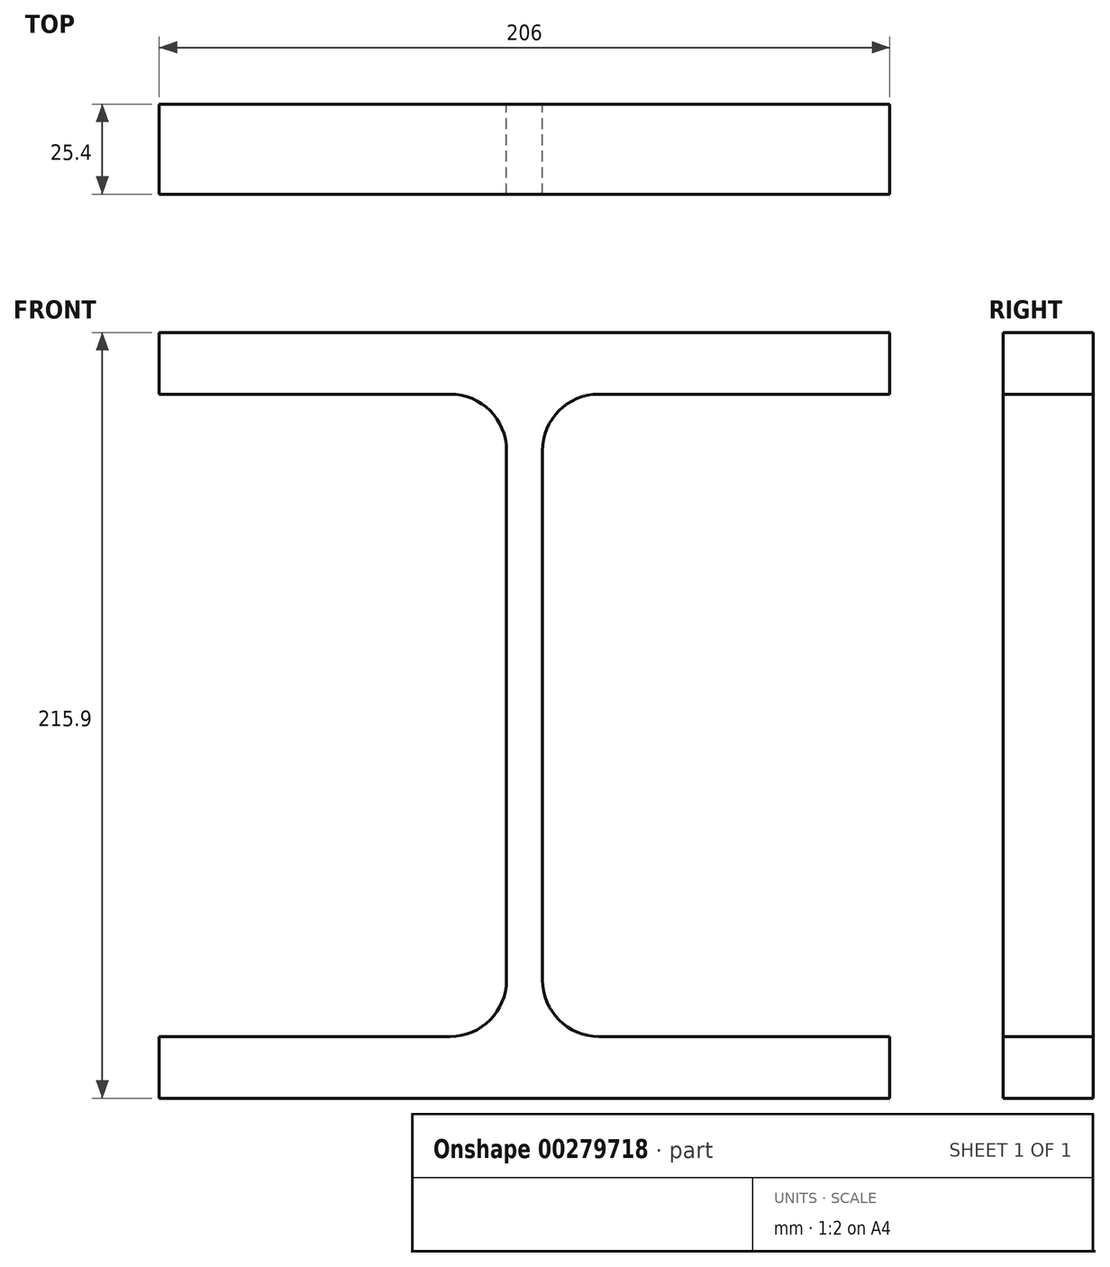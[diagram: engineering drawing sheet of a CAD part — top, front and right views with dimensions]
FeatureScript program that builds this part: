
annotation { "Feature Type Name" : "Feature", "Feature Type Description" : "" }
export const myFeature = defineFeature(function(context is Context, id is Id, definition is map)
    precondition{}
    {
        {
            var Q0;
            Q0=qCreatedBy(makeId("Front.planeOp"),FACE);
            var sketch = newSketch(context, id + "F0", { "sketchPlane" : qUnion([Q0])});
            skLineSegment(sketch, "E0.bottom", {"start": v(-103, 107.95) * mm, "end": v(103, 107.95) * mm});
            skLineSegment(sketch, "E0.top", {"start": v(-103, -107.95) * mm, "end": v(103, -107.95) * mm});
            skLineSegment(sketch, "E0.left", {"start": v(-103, 107.95) * mm, "end": v(-103, -107.95) * mm, "construction": true});
            skLineSegment(sketch, "E0.right", {"start": v(103, 107.95) * mm, "end": v(103, -107.95) * mm, "construction": true});
            skPoint(sketch, "E0.middle", {"position": v(0, 0) * mm});
            skLineSegment(sketch, "E1", {"start": v(-103, 107.95) * mm, "end": v(-103, 90.55) * mm});
            skLineSegment(sketch, "E2", {"start": v(-103, 90.55) * mm, "end": v(-20.95, 90.55) * mm});
            skLineSegment(sketch, "E3", {"start": v(-5.08, 74.68) * mm, "end": v(-5.08, -74.68) * mm});
            skLineSegment(sketch, "E4", {"start": v(-20.95, -90.55) * mm, "end": v(-103, -90.55) * mm});
            skLineSegment(sketch, "E5", {"start": v(-103, -90.55) * mm, "end": v(-103, -107.95) * mm});
            skLineSegment(sketch, "E6", {"start": v(103, 107.95) * mm, "end": v(103, 90.55) * mm});
            skLineSegment(sketch, "E7", {"start": v(103, 90.55) * mm, "end": v(20.95, 90.55) * mm});
            skLineSegment(sketch, "E8", {"start": v(5.08, 74.68) * mm, "end": v(5.08, -74.68) * mm});
            skLineSegment(sketch, "E9", {"start": v(20.96, -90.55) * mm, "end": v(103, -90.55) * mm});
            skLineSegment(sketch, "E10", {"start": v(103, -90.55) * mm, "end": v(103, -107.95) * mm});
            skPoint(sketch, "E11.visualSharp", {"position": v(-5.08, 90.55) * mm});
            skArc(sketch, "E11.filletArc", {"start": v(-5.08, 74.68) * mm, "mid": v(-9.73, 85.9) * mm, "end": v(-20.95, 90.55) * mm});
            skPoint(sketch, "E12.visualSharp", {"position": v(5.08, 90.55) * mm});
            skArc(sketch, "E12.filletArc", {"start": v(20.95, 90.55) * mm, "mid": v(9.73, 85.9) * mm, "end": v(5.08, 74.68) * mm});
            skPoint(sketch, "E13.visualSharp", {"position": v(5.08, -90.55) * mm});
            skArc(sketch, "E13.filletArc", {"start": v(5.08, -74.68) * mm, "mid": v(9.73, -85.9) * mm, "end": v(20.96, -90.55) * mm});
            skPoint(sketch, "E14.visualSharp", {"position": v(-5.08, -90.55) * mm});
            skArc(sketch, "E14.filletArc", {"start": v(-20.95, -90.55) * mm, "mid": v(-9.73, -85.9) * mm, "end": v(-5.08, -74.68) * mm});
            skSolve(sketch);
        }
        {
            var Q0;
            Q0 = qSketchRegion(id + "F0", true);
            extrude(context, id + "F1", {"entities" : qUnion([Q0]), "depth" : 25.4 * mm});
        }
    });
